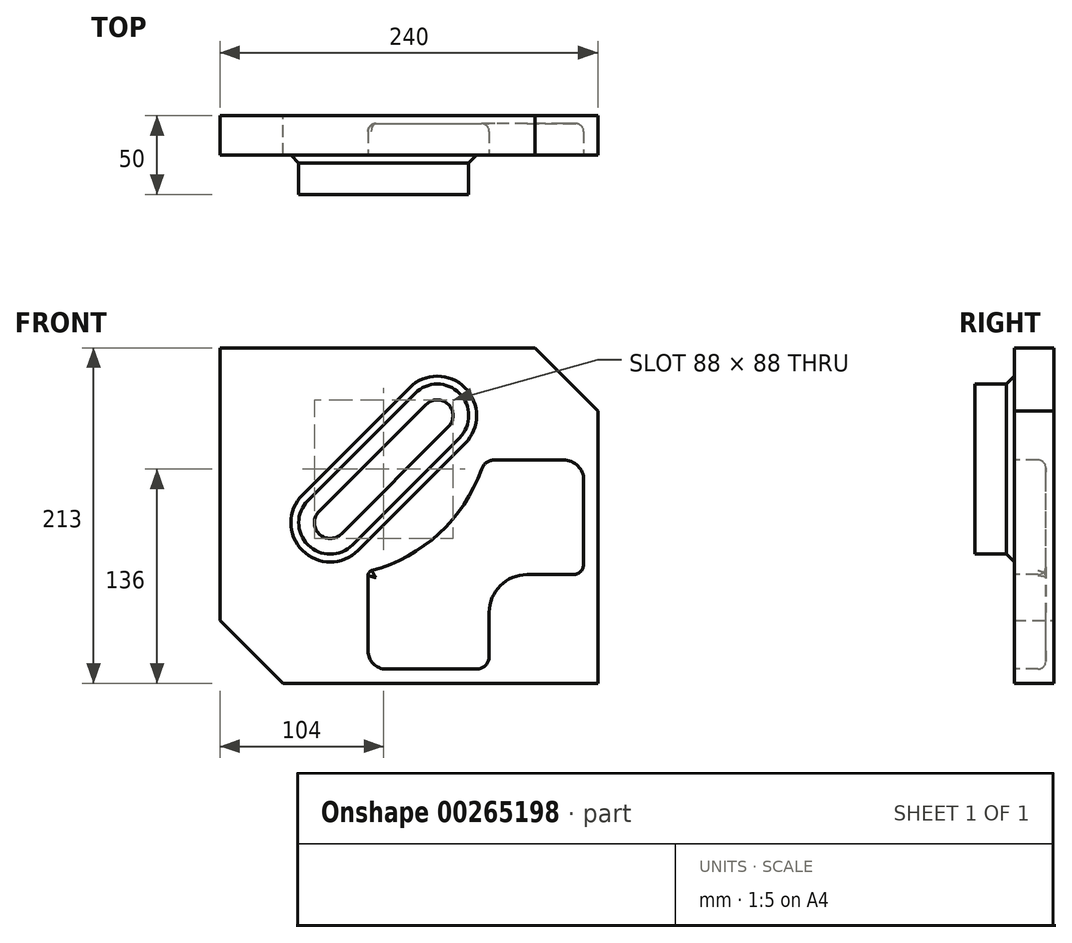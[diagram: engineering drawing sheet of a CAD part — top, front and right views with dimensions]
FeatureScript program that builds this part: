
annotation { "Feature Type Name" : "Feature", "Feature Type Description" : "" }
export const myFeature = defineFeature(function(context is Context, id is Id, definition is map)
    precondition{}
    {
        {
            var Q0;
            Q0=qCreatedBy(makeId("Front.planeOp"),FACE);
            var sketch = newSketch(context, id + "F0", { "sketchPlane" : qUnion([Q0])});
            skLineSegment(sketch, "E0", {"start": v(0, 0) * mm, "end": v(0, 173) * mm});
            skLineSegment(sketch, "E1", {"start": v(0, 173) * mm, "end": v(-40, 213) * mm});
            skLineSegment(sketch, "E2", {"start": v(-40, 213) * mm, "end": v(-240, 213) * mm});
            skLineSegment(sketch, "E3", {"start": v(-240, 40) * mm, "end": v(-200, 0) * mm});
            skLineSegment(sketch, "E4", {"start": v(-200, 0) * mm, "end": v(0, 0) * mm});
            skLineSegment(sketch, "E5", {"start": v(-240, 213) * mm, "end": v(-240, 40) * mm});
            skSolve(sketch);
        }
        {
            var Q0;
            Q0=makeQuery(id+"F0.imprint","IMPRINT",FACE,{"disambiguationData":[TD([[makeQuery(id+"F0.imprint","IMPRINT",EDGE,{"derivedFrom":sQuery(id+"F0.wireOp",EDGE,"E0")}),1.0]])]});
            var sketch = newSketch(context, id + "F1", { "sketchPlane" : qUnion([Q0])});
            skLineSegment(sketch, "E6.JFZ.JFZ", {"start": v(-170, 102) * mm, "end": v(-102, 170) * mm, "construction": true});
            skArc(sketch, "E6.0.startCap", {"start": v(-162.93, 94.93) * mm, "mid": v(-177.07, 94.93) * mm, "end": v(-177.07, 109.07) * mm});
            skArc(sketch, "E6.0.endCap", {"start": v(-109.07, 177.07) * mm, "mid": v(-94.93, 177.07) * mm, "end": v(-94.93, 162.93) * mm});
            skLineSegment(sketch, "E6.0.left", {"start": v(-177.07, 109.07) * mm, "end": v(-109.07, 177.07) * mm});
            skLineSegment(sketch, "E6.0.right", {"start": v(-162.93, 94.93) * mm, "end": v(-94.93, 162.93) * mm});
            skArc(sketch, "E7.0.startCap", {"start": v(-155.86, 87.86) * mm, "mid": v(-184.14, 87.86) * mm, "end": v(-184.14, 116.14) * mm});
            skArc(sketch, "E7.0.endCap", {"start": v(-116.14, 184.14) * mm, "mid": v(-87.86, 184.14) * mm, "end": v(-87.86, 155.86) * mm});
            skLineSegment(sketch, "E7.0.left", {"start": v(-184.14, 116.14) * mm, "end": v(-116.14, 184.14) * mm});
            skLineSegment(sketch, "E7.0.right", {"start": v(-155.86, 87.86) * mm, "end": v(-87.86, 155.86) * mm});
            skArc(sketch, "E8", {"start": v(-143.6, 71.54) * mm, "mid": v(-100.85, 95.1) * mm, "end": v(-73.95, 135.84) * mm});
            skLineSegment(sketch, "E9", {"start": v(-134.44, 9) * mm, "end": v(-76.94, 9) * mm});
            skLineSegment(sketch, "E10", {"start": v(-69, 16.94) * mm, "end": v(-69, 45) * mm});
            skLineSegment(sketch, "E11", {"start": v(-45, 69) * mm, "end": v(-15.68, 69) * mm});
            skLineSegment(sketch, "E12", {"start": v(-9, 75.68) * mm, "end": v(-9, 129.04) * mm});
            skLineSegment(sketch, "E13", {"start": v(-21.8, 141.84) * mm, "end": v(-65.45, 141.84) * mm});
            skLineSegment(sketch, "E14", {"start": v(-146, 20.56) * mm, "end": v(-146, 68.42) * mm});
            skArc(sketch, "E15", {"start": v(-45, 69) * mm, "mid": v(-61.97, 61.97) * mm, "end": v(-69, 45) * mm});
            skArc(sketch, "E16", {"start": v(-143.6, 71.54) * mm, "mid": v(-145.33, 70.38) * mm, "end": v(-146, 68.42) * mm});
            skArc(sketch, "E17", {"start": v(-65.45, 141.84) * mm, "mid": v(-70.66, 140.19) * mm, "end": v(-73.95, 135.84) * mm});
            skArc(sketch, "E18", {"start": v(-9, 129.04) * mm, "mid": v(-12.75, 138.09) * mm, "end": v(-21.8, 141.84) * mm});
            skArc(sketch, "E19", {"start": v(-15.68, 69) * mm, "mid": v(-10.96, 70.96) * mm, "end": v(-9, 75.68) * mm});
            skArc(sketch, "E20", {"start": v(-76.94, 9) * mm, "mid": v(-71.33, 11.33) * mm, "end": v(-69, 16.94) * mm});
            skArc(sketch, "E21", {"start": v(-146, 20.56) * mm, "mid": v(-142.62, 12.38) * mm, "end": v(-134.44, 9) * mm});
            skPoint(sketch, "E22.orphan", {"position": v(-9, 69) * mm});
            skPoint(sketch, "E23.orphan", {"position": v(-69, 9) * mm});
            skPoint(sketch, "E24.orphan", {"position": v(-146, 9) * mm});
            skSolve(sketch);
        }
        {
            var Q0;
            Q0 = qSketchRegion(id + "F0", true);
            extrude(context, id + "F2", {"entities" : qUnion([Q0]), "depth" : 25 * mm});
        }
        {
            var Q0;
            Q0 = qSketchRegion(id + "F1", true);
            extrude(context, id + "F3", {"entities" : qUnion([Q0]), "operationType" : NewBodyOperationType.ADD, "depth" : 50 * mm});
        }
        {
            var Q0;
            Q0=makeQuery(id+"F3.boolean.opBoolean","SPLIT",FACE,{"disambiguationData":[TD([makeQuery(id+"F3.opExtrude","SWEPT_FACE",FACE,{"disambiguationData":[OSD([sQuery(id+"F1.wireOp",EDGE,"E6.0.startCap")])]})])],"derivedFrom":makeQuery(id+"F2.opExtrude","CAP_FACE",FACE,{"disambiguationData":[OSD([sQuery(id+"F0.wireOp",EDGE,"E0"),sQuery(id+"F0.wireOp",EDGE,"E1"),sQuery(id+"F0.wireOp",EDGE,"E2"),sQuery(id+"F0.wireOp",EDGE,"E3"),sQuery(id+"F0.wireOp",EDGE,"E4"),sQuery(id+"F0.wireOp",EDGE,"E5")])],"isStart":false})});
            extrude(context, id + "F4", {"entities" : qUnion([Q0]), "operationType" : NewBodyOperationType.REMOVE, "oppositeDirection" : true, "depth" : 25 * mm});
        }
        {
            var Q0;
            Q0=makeQuery(id+"F3.boolean.opBoolean","INTERSECT",EDGE,{"derivedFrom":[makeQuery(id+"F2.opExtrude","CAP_FACE",FACE,{"disambiguationData":[OSD([sQuery(id+"F0.wireOp",EDGE,"E0"),sQuery(id+"F0.wireOp",EDGE,"E1"),sQuery(id+"F0.wireOp",EDGE,"E2"),sQuery(id+"F0.wireOp",EDGE,"E3"),sQuery(id+"F0.wireOp",EDGE,"E4"),sQuery(id+"F0.wireOp",EDGE,"E5")])],"isStart":false}),makeQuery(id+"F3.opExtrude","SWEPT_FACE",FACE,{"disambiguationData":[OSD([sQuery(id+"F1.wireOp",EDGE,"E7.0.right")])]})]});
            chamfer(context, id + "F5", {"entities" : qUnion([Q0]), "width" : 5 * mm, "tangentPropagation" : true});
        }
        {
            var Q0;
            Q0=makeQuery(id+"F3.opExtrude","CAP_FACE",FACE,{"disambiguationData":[OSD([sQuery(id+"F1.wireOp",EDGE,"E8"),sQuery(id+"F1.wireOp",EDGE,"E9"),sQuery(id+"F1.wireOp",EDGE,"E10"),sQuery(id+"F1.wireOp",EDGE,"E11"),sQuery(id+"F1.wireOp",EDGE,"E12"),sQuery(id+"F1.wireOp",EDGE,"E13"),sQuery(id+"F1.wireOp",EDGE,"E14"),sQuery(id+"F1.wireOp",EDGE,"E15"),sQuery(id+"F1.wireOp",EDGE,"E16"),sQuery(id+"F1.wireOp",EDGE,"E17"),sQuery(id+"F1.wireOp",EDGE,"E18"),sQuery(id+"F1.wireOp",EDGE,"E19"),sQuery(id+"F1.wireOp",EDGE,"E20"),sQuery(id+"F1.wireOp",EDGE,"E21")])],"isStart":false});
            extrude(context, id + "F6", {"entities" : qUnion([Q0]), "operationType" : NewBodyOperationType.ADD, "oppositeDirection" : true, "depth" : 45 * mm});
        }
        {
            var Q0;
            Q0=makeQuery(id+"F3.opExtrude","CAP_FACE",FACE,{"disambiguationData":[OSD([sQuery(id+"F1.wireOp",EDGE,"E8"),sQuery(id+"F1.wireOp",EDGE,"E9"),sQuery(id+"F1.wireOp",EDGE,"E10"),sQuery(id+"F1.wireOp",EDGE,"E11"),sQuery(id+"F1.wireOp",EDGE,"E12"),sQuery(id+"F1.wireOp",EDGE,"E13"),sQuery(id+"F1.wireOp",EDGE,"E14"),sQuery(id+"F1.wireOp",EDGE,"E15"),sQuery(id+"F1.wireOp",EDGE,"E16"),sQuery(id+"F1.wireOp",EDGE,"E17"),sQuery(id+"F1.wireOp",EDGE,"E18"),sQuery(id+"F1.wireOp",EDGE,"E19"),sQuery(id+"F1.wireOp",EDGE,"E20"),sQuery(id+"F1.wireOp",EDGE,"E21")])],"isStart":false});
            extrude(context, id + "F7", {"entities" : qUnion([Q0]), "operationType" : NewBodyOperationType.REMOVE, "oppositeDirection" : true, "depth" : 45 * mm});
        }
        {
            var Q0;
            Q0=makeQuery(id+"F3.boolean.opBoolean","INTERSECT",EDGE,{"derivedFrom":[makeQuery(id+"F2.opExtrude","CAP_FACE",FACE,{"disambiguationData":[OSD([sQuery(id+"F0.wireOp",EDGE,"E0"),sQuery(id+"F0.wireOp",EDGE,"E1"),sQuery(id+"F0.wireOp",EDGE,"E2"),sQuery(id+"F0.wireOp",EDGE,"E3"),sQuery(id+"F0.wireOp",EDGE,"E4"),sQuery(id+"F0.wireOp",EDGE,"E5")])],"isStart":false}),makeQuery(id+"F3.opExtrude","SWEPT_FACE",FACE,{"disambiguationData":[OSD([sQuery(id+"F1.wireOp",EDGE,"E8")])]})]});
            var Q1;
            Q1=makeQuery(id+"F7.boolean.opBoolean","COPY",EDGE,{"derivedFrom":makeQuery(id+"F7.opExtrude","CAP_EDGE",EDGE,{"disambiguationData":[OSD([sQuery(id+"F1.wireOp",EDGE,"E8")])],"isStart":false})});
            fillet(context, id + "F8", {"entities" : qUnion([Q0, Q1]), "radius" : 5 * mm, "tangentPropagation" : true, "allowEdgeOverflow" : false});
        }
    });
